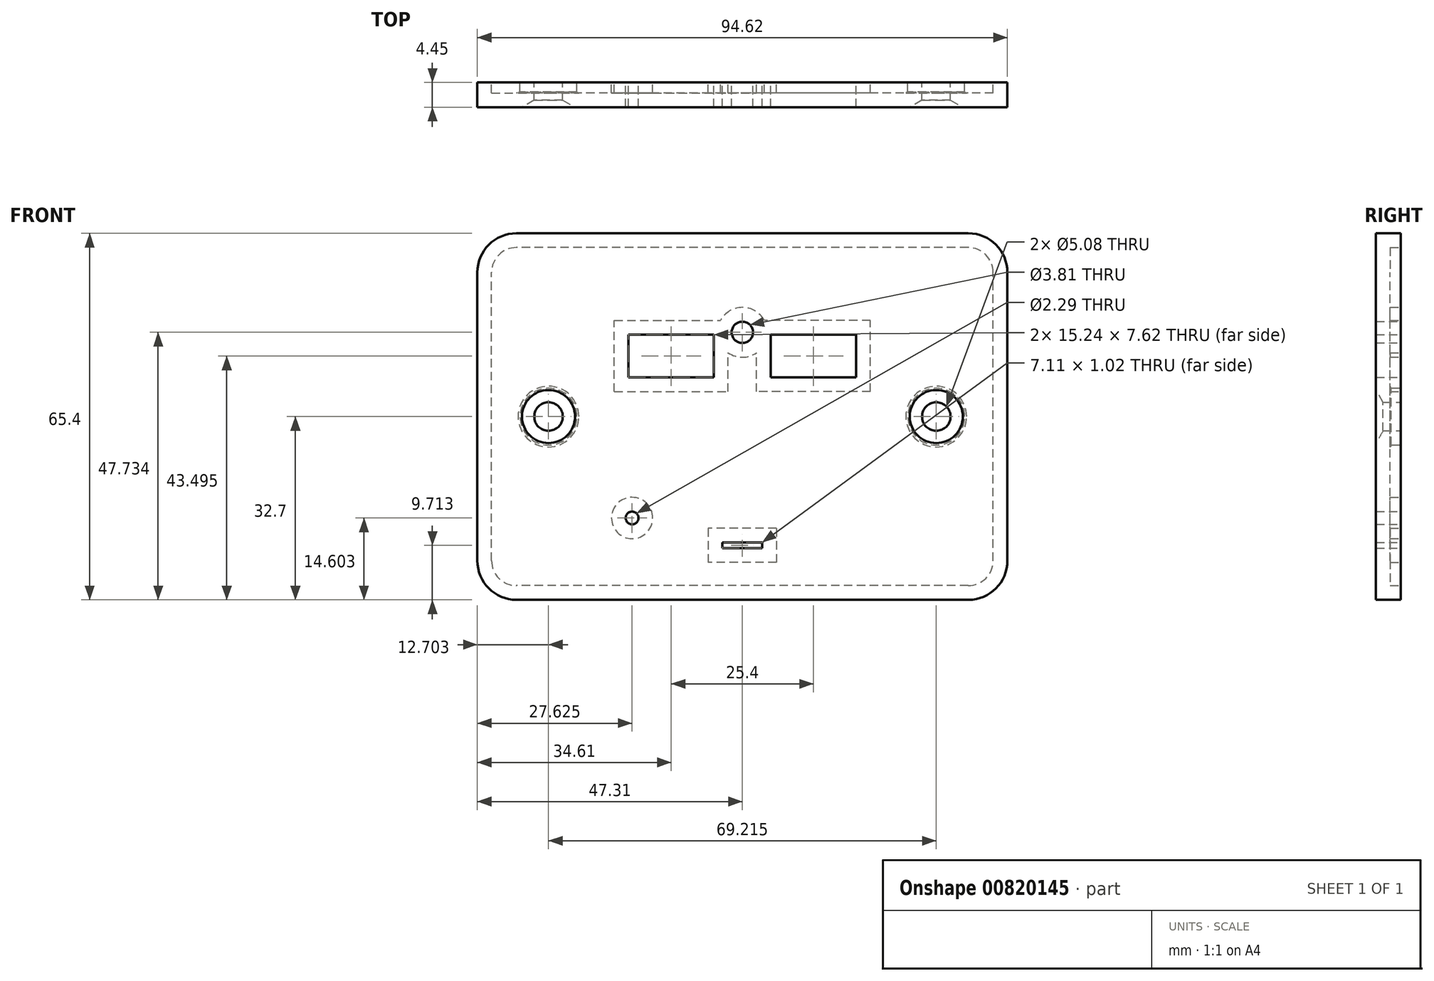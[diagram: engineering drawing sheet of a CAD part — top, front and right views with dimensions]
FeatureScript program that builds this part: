
annotation { "Feature Type Name" : "Feature", "Feature Type Description" : "" }
export const myFeature = defineFeature(function(context is Context, id is Id, definition is map)
    precondition{}
    {
        {
            var Q0;
            Q0=qCreatedBy(makeId("Front.planeOp"),FACE);
            var sketch = newSketch(context, id + "F0", { "sketchPlane" : qUnion([Q0])});
            skLineSegment(sketch, "E0.bottom", {"start": v(47.3, -32.7) * mm, "end": v(-47.3, -32.7) * mm});
            skLineSegment(sketch, "E0.top", {"start": v(47.3, 32.7) * mm, "end": v(-47.3, 32.7) * mm});
            skLineSegment(sketch, "E0.left", {"start": v(47.3, -32.7) * mm, "end": v(47.3, 32.7) * mm});
            skLineSegment(sketch, "E0.right", {"start": v(-47.3, -32.7) * mm, "end": v(-47.3, 32.7) * mm});
            skPoint(sketch, "E0.middle", {"position": v(0, 0) * mm});
            skLineSegment(sketch, "E1.bottom", {"start": v(24.77, -23.5) * mm, "end": v(-24.77, -23.5) * mm});
            skLineSegment(sketch, "E1.top", {"start": v(24.77, 23.5) * mm, "end": v(-24.77, 23.5) * mm});
            skLineSegment(sketch, "E1.left", {"start": v(24.77, -23.5) * mm, "end": v(24.77, 23.5) * mm});
            skLineSegment(sketch, "E1.right", {"start": v(-24.77, -23.5) * mm, "end": v(-24.77, 23.5) * mm});
            skLineSegment(sketch, "E2.0", {"start": v(23.75, 22.48) * mm, "end": v(-23.75, 22.48) * mm});
            skLineSegment(sketch, "E2.1", {"start": v(23.75, -22.48) * mm, "end": v(23.75, 22.48) * mm});
            skLineSegment(sketch, "E2.2", {"start": v(23.75, -22.48) * mm, "end": v(-23.75, -22.48) * mm});
            skLineSegment(sketch, "E2.3", {"start": v(-23.75, -22.48) * mm, "end": v(-23.75, 22.48) * mm});
            skLineSegment(sketch, "E3.bottom", {"start": v(20.32, 6.99) * mm, "end": v(5.08, 6.99) * mm});
            skLineSegment(sketch, "E3.top", {"start": v(20.32, 14.6) * mm, "end": v(5.08, 14.6) * mm});
            skLineSegment(sketch, "E3.left", {"start": v(20.32, 6.99) * mm, "end": v(20.32, 14.6) * mm});
            skLineSegment(sketch, "E3.right", {"start": v(5.08, 6.99) * mm, "end": v(5.08, 14.6) * mm});
            skPoint(sketch, "E3.middle", {"position": v(12.7, 10.8) * mm});
            skLineSegment(sketch, "E4.MirrorCS", {"start": v(-20.32, 6.99) * mm, "end": v(-20.32, 14.6) * mm});
            skLineSegment(sketch, "E5.MirrorCS", {"start": v(-5.08, 6.99) * mm, "end": v(-5.08, 14.6) * mm});
            skLineSegment(sketch, "E6.MirrorCS", {"start": v(-20.32, 6.99) * mm, "end": v(-5.08, 6.99) * mm});
            skLineSegment(sketch, "E7.MirrorCS", {"start": v(-20.32, 14.6) * mm, "end": v(-5.08, 14.6) * mm});
            skCircle(sketch, "E8", {"center": v(-19.69, 18.1) * mm, "radius": 2.41 * mm});
            skCircle(sketch, "E9.0", {"center": v(-19.69, 18.1) * mm, "radius": 1.14 * mm});
            skCircle(sketch, "E10.MirrorC", {"center": v(19.69, 18.1) * mm, "radius": 1.14 * mm});
            skCircle(sketch, "E11.MirrorC", {"center": v(19.69, 18.1) * mm, "radius": 2.41 * mm});
            skCircle(sketch, "E12.MirrorC", {"center": v(-19.69, -18.1) * mm, "radius": 2.41 * mm});
            skCircle(sketch, "E13.MirrorC", {"center": v(-19.69, -18.1) * mm, "radius": 1.14 * mm});
            skCircle(sketch, "E14.MirrorC", {"center": v(19.69, -18.1) * mm, "radius": 1.14 * mm});
            skCircle(sketch, "E15.MirrorC", {"center": v(19.69, -18.1) * mm, "radius": 2.41 * mm});
            skCircle(sketch, "E16", {"center": v(0, 15.03) * mm, "radius": 1.9 * mm});
            skCircle(sketch, "E17", {"center": v(-34.6, 0) * mm, "radius": 2.54 * mm});
            skCircle(sketch, "E18", {"center": v(34.6, 0) * mm, "radius": 2.54 * mm});
            skLineSegment(sketch, "E19.bottom", {"start": v(3.56, -22.48) * mm, "end": v(-3.56, -22.48) * mm});
            skLineSegment(sketch, "E19.top", {"start": v(3.56, -23.5) * mm, "end": v(-3.56, -23.5) * mm});
            skLineSegment(sketch, "E19.left", {"start": v(3.56, -22.48) * mm, "end": v(3.56, -23.5) * mm});
            skLineSegment(sketch, "E19.right", {"start": v(-3.56, -22.48) * mm, "end": v(-3.56, -23.5) * mm});
            skPoint(sketch, "E19.middle", {"position": v(0, -22.99) * mm});
            skPoint(sketch, "E20", {"position": v(0, -22.48) * mm});
            skLineSegment(sketch, "E21.0", {"start": v(43.5, 28.9) * mm, "end": v(-43.5, 28.9) * mm});
            skLineSegment(sketch, "E21.1", {"start": v(43.5, -28.9) * mm, "end": v(43.5, 28.9) * mm});
            skLineSegment(sketch, "E21.2", {"start": v(43.5, -28.9) * mm, "end": v(-43.5, -28.9) * mm});
            skLineSegment(sketch, "E21.3", {"start": v(-43.5, -28.9) * mm, "end": v(-43.5, 28.9) * mm});
            skCircle(sketch, "E22.0", {"center": v(-34.6, 0) * mm, "radius": 5.08 * mm});
            skCircle(sketch, "E23.0", {"center": v(34.6, 0) * mm, "radius": 5.08 * mm});
            skSolve(sketch);
        }
        {
            var Q0;
            Q0=makeQuery(id+"F0.imprint","IMPRINT",FACE,{"disambiguationData":[TD([[makeQuery(id+"F0.imprint","IMPRINT",EDGE,{"derivedFrom":sQuery(id+"F0.wireOp",EDGE,"E1.bottom")}),-1.0]])]});
            var Q1;
            Q1=makeQuery(id+"F0.imprint","IMPRINT",FACE,{"disambiguationData":[TD([[makeQuery(id+"F0.imprint","IMPRINT",EDGE,{"derivedFrom":sQuery(id+"F0.wireOp",EDGE,"E0.bottom")}),-1.0]])]});
            var Q2;
            Q2=makeQuery(id+"F0.imprint","IMPRINT",FACE,{"disambiguationData":[TD([[makeQuery(id+"F0.imprint","IMPRINT",EDGE,{"derivedFrom":sQuery(id+"F0.wireOp",EDGE,"E2.0")}),1.0]])]});
            var Q3;
            Q3=makeQuery(id+"F0.imprint","IMPRINT",FACE,{"disambiguationData":[TD([[makeQuery(id+"F0.imprint","IMPRINT",EDGE,{"derivedFrom":sQuery(id+"F0.wireOp",EDGE,"E8")}),1.0]])]});
            var Q4;
            Q4=makeQuery(id+"F0.imprint","IMPRINT",FACE,{"disambiguationData":[TD([[makeQuery(id+"F0.imprint","IMPRINT",EDGE,{"derivedFrom":sQuery(id+"F0.wireOp",EDGE,"E12.MirrorC")}),-1.0]])]});
            var Q5;
            Q5=makeQuery(id+"F0.imprint","IMPRINT",FACE,{"disambiguationData":[TD([[makeQuery(id+"F0.imprint","IMPRINT",EDGE,{"derivedFrom":sQuery(id+"F0.wireOp",EDGE,"E19.bottom")}),1.0]])]});
            var Q6;
            Q6=makeQuery(id+"F0.imprint","IMPRINT",FACE,{"disambiguationData":[TD([[makeQuery(id+"F0.imprint","IMPRINT",EDGE,{"derivedFrom":sQuery(id+"F0.wireOp",EDGE,"E9.0")}),1.0]])]});
            var Q7;
            Q7=makeQuery(id+"F0.imprint","IMPRINT",FACE,{"disambiguationData":[TD([[makeQuery(id+"F0.imprint","IMPRINT",EDGE,{"derivedFrom":sQuery(id+"F0.wireOp",EDGE,"E13.MirrorC")}),-1.0]])]});
            var Q8;
            Q8=makeQuery(id+"F0.imprint","IMPRINT",FACE,{"disambiguationData":[TD([[makeQuery(id+"F0.imprint","IMPRINT",EDGE,{"derivedFrom":sQuery(id+"F0.wireOp",EDGE,"E14.MirrorC")}),1.0]])]});
            var Q9;
            Q9=makeQuery(id+"F0.imprint","IMPRINT",FACE,{"disambiguationData":[TD([[makeQuery(id+"F0.imprint","IMPRINT",EDGE,{"derivedFrom":sQuery(id+"F0.wireOp",EDGE,"E14.MirrorC")}),-1.0]])]});
            var Q10;
            Q10=makeQuery(id+"F0.imprint","IMPRINT",FACE,{"disambiguationData":[TD([[makeQuery(id+"F0.imprint","IMPRINT",EDGE,{"derivedFrom":sQuery(id+"F0.wireOp",EDGE,"E10.MirrorC")}),1.0]])]});
            var Q11;
            Q11=makeQuery(id+"F0.imprint","IMPRINT",FACE,{"disambiguationData":[TD([[makeQuery(id+"F0.imprint","IMPRINT",EDGE,{"derivedFrom":sQuery(id+"F0.wireOp",EDGE,"E10.MirrorC")}),-1.0]])]});
            var Q12;
            Q12=makeQuery(id+"F0.imprint","IMPRINT",FACE,{"disambiguationData":[TD([[makeQuery(id+"F0.imprint","IMPRINT",EDGE,{"derivedFrom":sQuery(id+"F0.wireOp",EDGE,"E1.top")}),-1.0]])]});
            var Q13;
            Q13=makeQuery(id+"F0.imprint","IMPRINT",FACE,{"disambiguationData":[TD([[makeQuery(id+"F0.imprint","IMPRINT",EDGE,{"derivedFrom":sQuery(id+"F0.wireOp",EDGE,"E18")}),-1.0]])]});
            var Q14;
            Q14=makeQuery(id+"F0.imprint","IMPRINT",FACE,{"disambiguationData":[TD([[makeQuery(id+"F0.imprint","IMPRINT",EDGE,{"derivedFrom":sQuery(id+"F0.wireOp",EDGE,"E17")}),-1.0]])]});
            extrude(context, id + "F1", {"entities" : qUnion([Q0, Q1, Q2, Q3, Q4, Q5, Q6, Q7, Q8, Q9, Q10, Q11, Q12, Q13, Q14]), "depth" : 4.44 * mm, "offsetDistance" : 25.4 * mm});
        }
        {
            var Q0;
            Q0=makeQuery(id+"F1.opExtrude","SWEPT_EDGE",EDGE,{"disambiguationData":[OSD([sQuery(id+"F0.wireOp",EDGE,"E0.top"),sQuery(id+"F0.wireOp",EDGE,"E0.right")])]});
            var Q1;
            Q1=makeQuery(id+"F1.opExtrude","SWEPT_EDGE",EDGE,{"disambiguationData":[OSD([sQuery(id+"F0.wireOp",EDGE,"E0.bottom"),sQuery(id+"F0.wireOp",EDGE,"E0.right")])]});
            var Q2;
            Q2=makeQuery(id+"F1.opExtrude","SWEPT_EDGE",EDGE,{"disambiguationData":[OSD([sQuery(id+"F0.wireOp",EDGE,"E0.top"),sQuery(id+"F0.wireOp",EDGE,"E0.left")])]});
            var Q3;
            Q3=makeQuery(id+"F1.opExtrude","SWEPT_EDGE",EDGE,{"disambiguationData":[OSD([sQuery(id+"F0.wireOp",EDGE,"E0.bottom"),sQuery(id+"F0.wireOp",EDGE,"E0.left")])]});
            fillet(context, id + "F2", {"entities" : qUnion([Q0, Q1, Q2, Q3]), "radius" : 7 * mm, "tangentPropagation" : true, "allowEdgeOverflow" : false});
        }
        {
            var Q0;
            Q0=makeQuery(id+"F1.opExtrude","CAP_EDGE",EDGE,{"disambiguationData":[OSD([sQuery(id+"F0.wireOp",EDGE,"E17")])],"isStart":false});
            var Q1;
            Q1=makeQuery(id+"F1.opExtrude","CAP_EDGE",EDGE,{"disambiguationData":[OSD([sQuery(id+"F0.wireOp",EDGE,"E18")])],"isStart":false});
            chamfer(context, id + "F3", {"entities" : qUnion([Q0, Q1]), "chamferType" : ChamferType.OFFSET_ANGLE, "width" : 1.27 * mm, "oppositeDirection" : false, "angle" : 60 * degree, "tangentPropagation" : true});
        }
        {
            var Q0;
            Q0=makeQuery(id+"F1.opExtrude","CAP_FACE",FACE,{"disambiguationData":[OSD([sQuery(id+"F0.wireOp",EDGE,"E0.bottom"),sQuery(id+"F0.wireOp",EDGE,"E0.top"),sQuery(id+"F0.wireOp",EDGE,"E0.left"),sQuery(id+"F0.wireOp",EDGE,"E0.right"),sQuery(id+"F0.wireOp",EDGE,"E3.bottom"),sQuery(id+"F0.wireOp",EDGE,"E3.top"),sQuery(id+"F0.wireOp",EDGE,"E3.left"),sQuery(id+"F0.wireOp",EDGE,"E3.right"),sQuery(id+"F0.wireOp",EDGE,"E4.MirrorCS"),sQuery(id+"F0.wireOp",EDGE,"E5.MirrorCS"),sQuery(id+"F0.wireOp",EDGE,"E6.MirrorCS"),sQuery(id+"F0.wireOp",EDGE,"E7.MirrorCS"),sQuery(id+"F0.wireOp",EDGE,"E16"),sQuery(id+"F0.wireOp",EDGE,"E17"),sQuery(id+"F0.wireOp",EDGE,"E18")])],"isStart":true});
            shell(context, id + "F4", {"entities" : qUnion([Q0]), "thickness" : 2.54 * mm});
        }
    });
